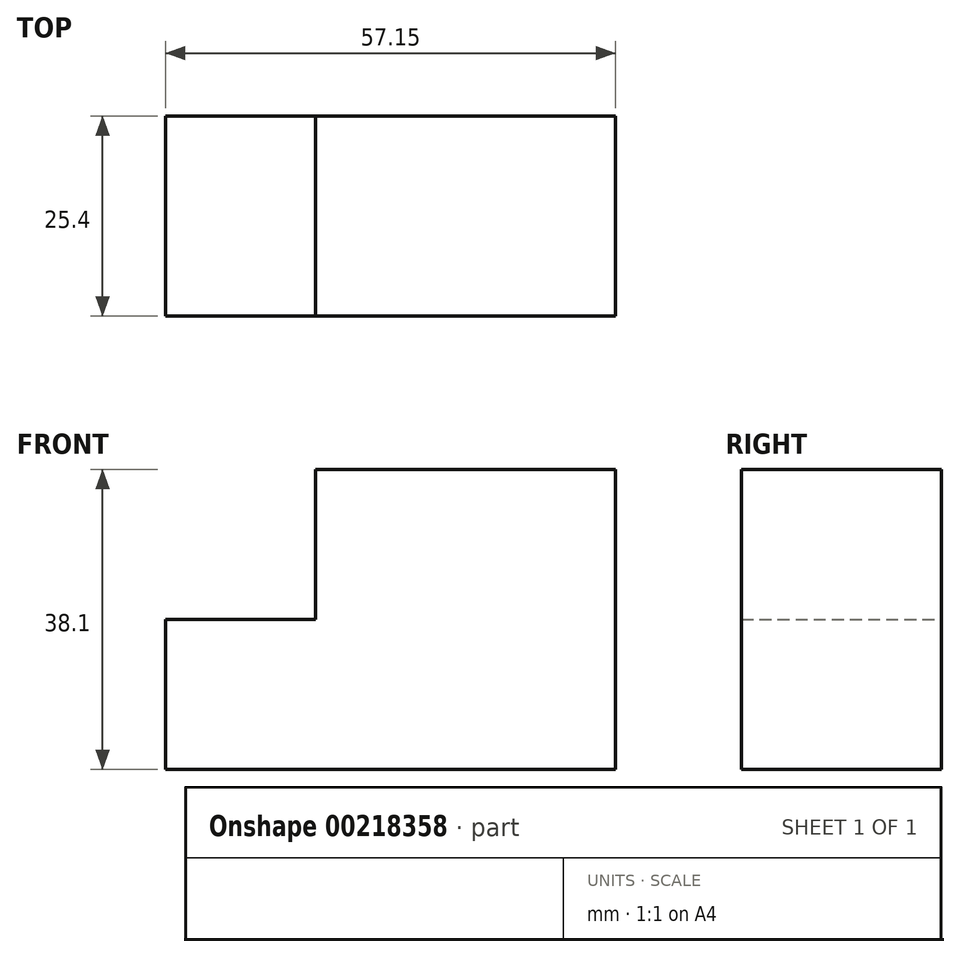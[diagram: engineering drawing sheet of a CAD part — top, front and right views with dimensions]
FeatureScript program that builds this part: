
annotation { "Feature Type Name" : "Feature", "Feature Type Description" : "" }
export const myFeature = defineFeature(function(context is Context, id is Id, definition is map)
    precondition{}
    {
        {
            var Q0;
            Q0=qCreatedBy(makeId("Front.planeOp"),FACE);
            var sketch = newSketch(context, id + "F0", { "sketchPlane" : qUnion([Q0])});
            skLineSegment(sketch, "E0.bottom", {"start": v(19.05, 19.05) * mm, "end": v(-19.05, 19.05) * mm});
            skLineSegment(sketch, "E0.top", {"start": v(19.05, -19.05) * mm, "end": v(-19.05, -19.05) * mm});
            skLineSegment(sketch, "E0.left", {"start": v(19.05, 19.05) * mm, "end": v(19.05, -19.05) * mm});
            skLineSegment(sketch, "E0.right", {"start": v(-19.05, 19.05) * mm, "end": v(-19.05, -19.05) * mm});
            skPoint(sketch, "E0.middle", {"position": v(0, 0) * mm});
            skLineSegment(sketch, "E1", {"start": v(-19.05, -19.05) * mm, "end": v(-38.1, -19.05) * mm});
            skLineSegment(sketch, "E2", {"start": v(-38.1, -19.05) * mm, "end": v(-38.1, 0) * mm});
            skLineSegment(sketch, "E3", {"start": v(-38.1, 0) * mm, "end": v(-19.05, 0) * mm});
            skSolve(sketch);
        }
        {
            var Q0;
            Q0 = qSketchRegion(id + "F0", true);
            extrude(context, id + "F1", {"entities" : qUnion([Q0]), "depth" : 25.4 * mm});
        }
    });
